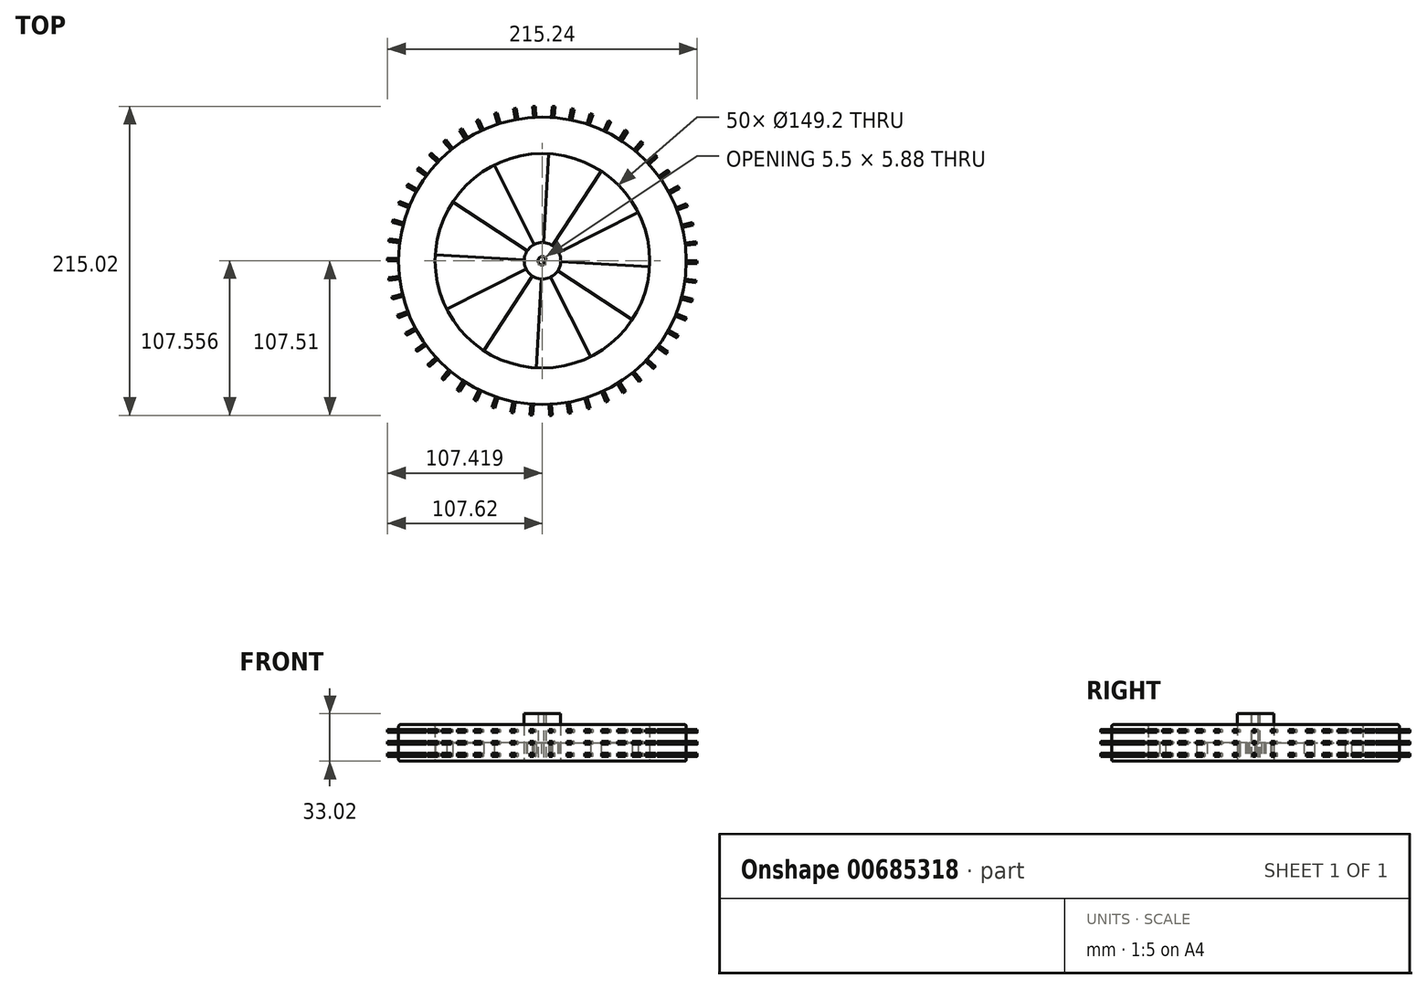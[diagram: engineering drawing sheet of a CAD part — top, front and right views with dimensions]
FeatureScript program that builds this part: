
annotation { "Feature Type Name" : "Feature", "Feature Type Description" : "" }
export const myFeature = defineFeature(function(context is Context, id is Id, definition is map)
    precondition{}
    {
        {
            var Q0;
            Q0=qCreatedBy(makeId("Top.planeOp"),FACE);
            var sketch = newSketch(context, id + "F0", { "sketchPlane" : qUnion([Q0])});
            skCircle(sketch, "E0", {"center": v(0, 0) * mm, "radius": 100 * mm});
            skCircle(sketch, "E1", {"center": v(0, 0) * mm, "radius": 74.6 * mm});
            skCircle(sketch, "E2", {"center": v(0, 0) * mm, "radius": 12.7 * mm});
            skLineSegment(sketch, "E3", {"start": v(0, 0) * mm, "end": v(-33.6, 66.6) * mm});
            skLineSegment(sketch, "E4", {"start": v(0, 0) * mm, "end": v(4.21, 74.48) * mm});
            skCircle(sketch, "E5", {"center": v(0, 0) * mm, "radius": 3 * mm});
            skLineSegment(sketch, "E6", {"start": v(2.55, 1.58) * mm, "end": v(0.78, -2.9) * mm});
            skSolve(sketch);
        }
        {
            var Q0;
            Q0=makeQuery(id+"F0.imprint","IMPRINT",FACE,{"disambiguationData":[TD([[makeQuery(id+"F0.imprint","IMPRINT",EDGE,{"derivedFrom":sQuery(id+"F0.wireOp",EDGE,"E0")}),1.0]])]});
            extrude(context, id + "F1", {"entities" : qUnion([Q0]), "depth" : 25.4 * mm, "offsetDistance" : 25.4 * mm});
        }
        {
            var Q0;
            {var subQ0=sQuery(id+"F0.wireOp",EDGE,"E3");var subQ1=sQuery(id+"F0.wireOp",EDGE,"E2");var subQ2=makeQuery(id+"F0.imprint","INTERSECT",VERTEX,{"derivedFrom":[subQ1,subQ0]});Q0=makeQuery(id+"F0.imprint","IMPRINT",FACE,{"disambiguationData":[TD([[makeQuery(id+"F0.imprint","IMPRINT",EDGE,{"disambiguationData":[TD([[subQ2,-1.0]])],"derivedFrom":subQ1}),1.0]])]});}
            var Q1;
            {var subQ0=sQuery(id+"F0.wireOp",EDGE,"E3");var subQ1=sQuery(id+"F0.wireOp",EDGE,"E2");var subQ2=makeQuery(id+"F0.imprint","INTERSECT",VERTEX,{"derivedFrom":[subQ1,subQ0]});Q1=makeQuery(id+"F0.imprint","IMPRINT",FACE,{"disambiguationData":[TD([[makeQuery(id+"F0.imprint","IMPRINT",EDGE,{"disambiguationData":[TD([[subQ2,1.0]])],"derivedFrom":subQ1}),1.0]])]});}
            var Q2;
            {var subQ0=sQuery(id+"F0.wireOp",EDGE,"E6");Q2=makeQuery(id+"F0.imprint","IMPRINT",FACE,{"disambiguationData":[TD([[makeQuery(id+"F0.imprint","IMPRINT",EDGE,{"derivedFrom":subQ0}),1.0]])]});}
            extrude(context, id + "F2", {"entities" : qUnion([Q0, Q1, Q2]), "depth" : 33.02 * mm, "offsetDistance" : 25.4 * mm});
        }
        {
            var Q0;
            {var subQ0=sQuery(id+"F0.wireOp",EDGE,"E3");var subQ1=sQuery(id+"F0.wireOp",EDGE,"E1");var subQ2=makeQuery(id+"F0.imprint","INTERSECT",VERTEX,{"derivedFrom":[subQ1,subQ0]});Q0=makeQuery(id+"F0.imprint","IMPRINT",FACE,{"disambiguationData":[TD([[makeQuery(id+"F0.imprint","IMPRINT",EDGE,{"disambiguationData":[TD([[subQ2,1.0]])],"derivedFrom":subQ1}),1.0]])]});}
            extrude(context, id + "F3", {"entities" : qUnion([Q0]), "depth" : 12.7 * mm, "offsetDistance" : 25.4 * mm});
        }
        {
            var Q0;
            Q0=makeQuery(id+"F3.opExtrude","SWEPT_BODY",BODY,{"disambiguationData":[OSD([sQuery(id+"F0.wireOp",EDGE,"E1"),sQuery(id+"F0.wireOp",EDGE,"E2"),sQuery(id+"F0.wireOp",EDGE,"E3"),sQuery(id+"F0.wireOp",EDGE,"E4")])]});
            var Q1;
            Q1=makeQuery(id+"F2.opExtrude","CAP_EDGE",EDGE,{"disambiguationData":[OSD([sQuery(id+"F0.wireOp",EDGE,"E2")])],"isStart":false});
            circularPattern(context, id + "F4", {"entities" : qUnion([Q0]), "axis" : qUnion([Q1]), "angle" : 360 * degree, "instanceCount" : 6, "equalSpace" : true});
        }
        {
            var Q0;
            Q0=makeQuery(id+"F1.opExtrude","CAP_FACE",FACE,{"disambiguationData":[OSD([sQuery(id+"F0.wireOp",EDGE,"E0"),sQuery(id+"F0.wireOp",EDGE,"E1")])],"isStart":false});
            var Q1;
            Q1=makeQuery(id+"F1.opExtrude","CAP_FACE",FACE,{"disambiguationData":[OSD([sQuery(id+"F0.wireOp",EDGE,"E0"),sQuery(id+"F0.wireOp",EDGE,"E1")])],"isStart":true});
            fillet(context, id + "F5", {"entities" : qUnion([Q0, Q1]), "radius" : 1.27 * mm, "tangentPropagation" : true, "allowEdgeOverflow" : false});
        }
        {
            var Q0;
            Q0=qCreatedBy(makeId("Front.planeOp"),FACE);
            var sketch = newSketch(context, id + "F6", { "sketchPlane" : qUnion([Q0])});
            skLineSegment(sketch, "E7", {"start": v(-100, 1.27) * mm, "end": v(-100, 24.13) * mm});
            skLineSegment(sketch, "E8", {"start": v(100, 24.13) * mm, "end": v(100, 1.27) * mm});
            skLineSegment(sketch, "E9.bottom", {"start": v(100, 22.1) * mm, "end": v(107.62, 22.1) * mm});
            skLineSegment(sketch, "E9.top", {"start": v(100, 20.07) * mm, "end": v(107.62, 20.07) * mm});
            skLineSegment(sketch, "E9.left", {"start": v(100, 22.1) * mm, "end": v(100, 20.07) * mm});
            skLineSegment(sketch, "E9.right", {"start": v(107.62, 22.1) * mm, "end": v(107.62, 20.07) * mm});
            skLineSegment(sketch, "E10.bottom", {"start": v(107.62, 11.68) * mm, "end": v(100, 11.68) * mm});
            skLineSegment(sketch, "E10.top", {"start": v(107.62, 13.72) * mm, "end": v(100, 13.72) * mm});
            skLineSegment(sketch, "E10.left", {"start": v(107.62, 11.68) * mm, "end": v(107.62, 13.72) * mm});
            skLineSegment(sketch, "E10.right", {"start": v(100, 11.68) * mm, "end": v(100, 13.72) * mm});
            skLineSegment(sketch, "E11.bottom", {"start": v(107.62, 3.3) * mm, "end": v(100, 3.3) * mm});
            skLineSegment(sketch, "E11.top", {"start": v(107.62, 5.33) * mm, "end": v(100, 5.33) * mm});
            skLineSegment(sketch, "E11.left", {"start": v(107.62, 3.3) * mm, "end": v(107.62, 5.33) * mm});
            skLineSegment(sketch, "E11.right", {"start": v(100, 3.3) * mm, "end": v(100, 5.33) * mm});
            skSolve(sketch);
        }
        {
            var Q0;
            Q0=makeQuery(id+"F6.imprint","IMPRINT",FACE,{"disambiguationData":[TD([[makeQuery(id+"F6.imprint","IMPRINT",EDGE,{"derivedFrom":sQuery(id+"F6.wireOp",EDGE,"E9.bottom")}),-1.0]])]});
            var Q1;
            Q1=makeQuery(id+"F6.imprint","IMPRINT",FACE,{"disambiguationData":[TD([[makeQuery(id+"F6.imprint","IMPRINT",EDGE,{"derivedFrom":sQuery(id+"F6.wireOp",EDGE,"E10.bottom")}),-1.0]])]});
            var Q2;
            Q2=makeQuery(id+"F6.imprint","IMPRINT",FACE,{"disambiguationData":[TD([[makeQuery(id+"F6.imprint","IMPRINT",EDGE,{"derivedFrom":sQuery(id+"F6.wireOp",EDGE,"E11.bottom")}),-1.0]])]});
            var Q3;
            Q3=makeQuery(id+"F2.opExtrude","SWEPT_FACE",FACE,{"disambiguationData":[OSD([sQuery(id+"F0.wireOp",EDGE,"E2")])]});
            revolve(context, id + "F7", {"operationType" : NewBodyOperationType.ADD, "entities" : qUnion([Q0, Q1, Q2]), "axis" : qUnion([Q3]), "revolveType" : RevolveType.ONE_DIRECTION, "angle" : 1 * degree});
        }
        {
            var Q0;
            Q0=makeQuery(id+"F1.opExtrude","SWEPT_BODY",BODY,{"disambiguationData":[OSD([sQuery(id+"F0.wireOp",EDGE,"E0"),sQuery(id+"F0.wireOp",EDGE,"E1")])]});
            var Q1;
            Q1=makeQuery(id+"F2.opExtrude","SWEPT_FACE",FACE,{"disambiguationData":[OSD([sQuery(id+"F0.wireOp",EDGE,"E2")])]});
            circularPattern(context, id + "F8", {"entities" : qUnion([Q0]), "axis" : qUnion([Q1]), "angle" : 360 * degree, "instanceCount" : 50, "equalSpace" : true});
        }
    });
